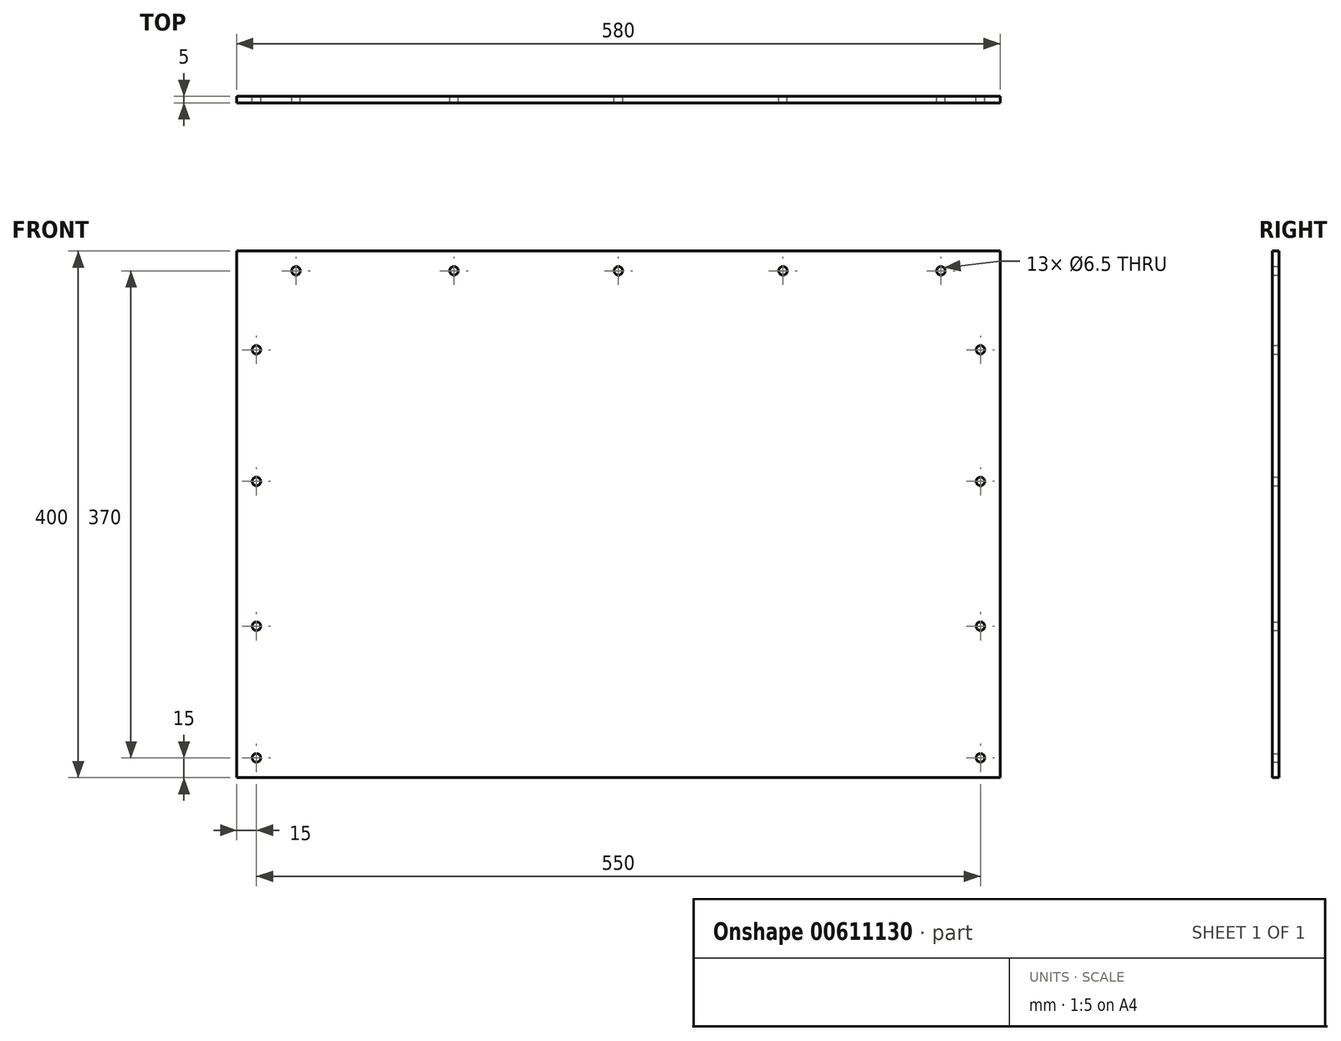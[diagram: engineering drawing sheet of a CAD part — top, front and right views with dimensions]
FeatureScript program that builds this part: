
annotation { "Feature Type Name" : "Feature", "Feature Type Description" : "" }
export const myFeature = defineFeature(function(context is Context, id is Id, definition is map)
    precondition{}
    {
        {
            var Q0;
            Q0=qCreatedBy(makeId("Front.planeOp"),FACE);
            var sketch = newSketch(context, id + "F0", { "sketchPlane" : qUnion([Q0])});
            skLineSegment(sketch, "E0.bottom", {"start": v(0, 0) * mm, "end": v(580, 0) * mm});
            skLineSegment(sketch, "E0.top", {"start": v(0, 400) * mm, "end": v(580, 400) * mm});
            skLineSegment(sketch, "E0.left", {"start": v(0, 0) * mm, "end": v(0, 400) * mm});
            skLineSegment(sketch, "E0.right", {"start": v(580, 0) * mm, "end": v(580, 400) * mm});
            skCircle(sketch, "E1", {"center": v(15, 325) * mm, "radius": 3.25 * mm});
            skCircle(sketch, "E2", {"center": v(15, 15) * mm, "radius": 3.25 * mm});
            skCircle(sketch, "E3", {"center": v(15, 115) * mm, "radius": 3.25 * mm});
            skCircle(sketch, "E4", {"center": v(15, 225) * mm, "radius": 3.25 * mm});
            skCircle(sketch, "E5", {"center": v(565, 15) * mm, "radius": 3.25 * mm});
            skCircle(sketch, "E6", {"center": v(565, 115) * mm, "radius": 3.25 * mm});
            skCircle(sketch, "E7", {"center": v(565, 225) * mm, "radius": 3.25 * mm});
            skCircle(sketch, "E8", {"center": v(565, 325) * mm, "radius": 3.25 * mm});
            skCircle(sketch, "E9", {"center": v(45, 385) * mm, "radius": 3.25 * mm});
            skCircle(sketch, "E10", {"center": v(290, 385) * mm, "radius": 3.25 * mm});
            skCircle(sketch, "E11", {"center": v(535, 385) * mm, "radius": 3.25 * mm});
            skCircle(sketch, "E12", {"center": v(415, 385) * mm, "radius": 3.25 * mm});
            skCircle(sketch, "E13", {"center": v(165, 385) * mm, "radius": 3.25 * mm});
            skSolve(sketch);
        }
        {
            var Q0;
            Q0 = qSketchRegion(id + "F0", true);
            extrude(context, id + "F1", {"entities" : qUnion([Q0]), "depth" : 5 * mm, "offsetDistance" : 25 * mm});
        }
    });
